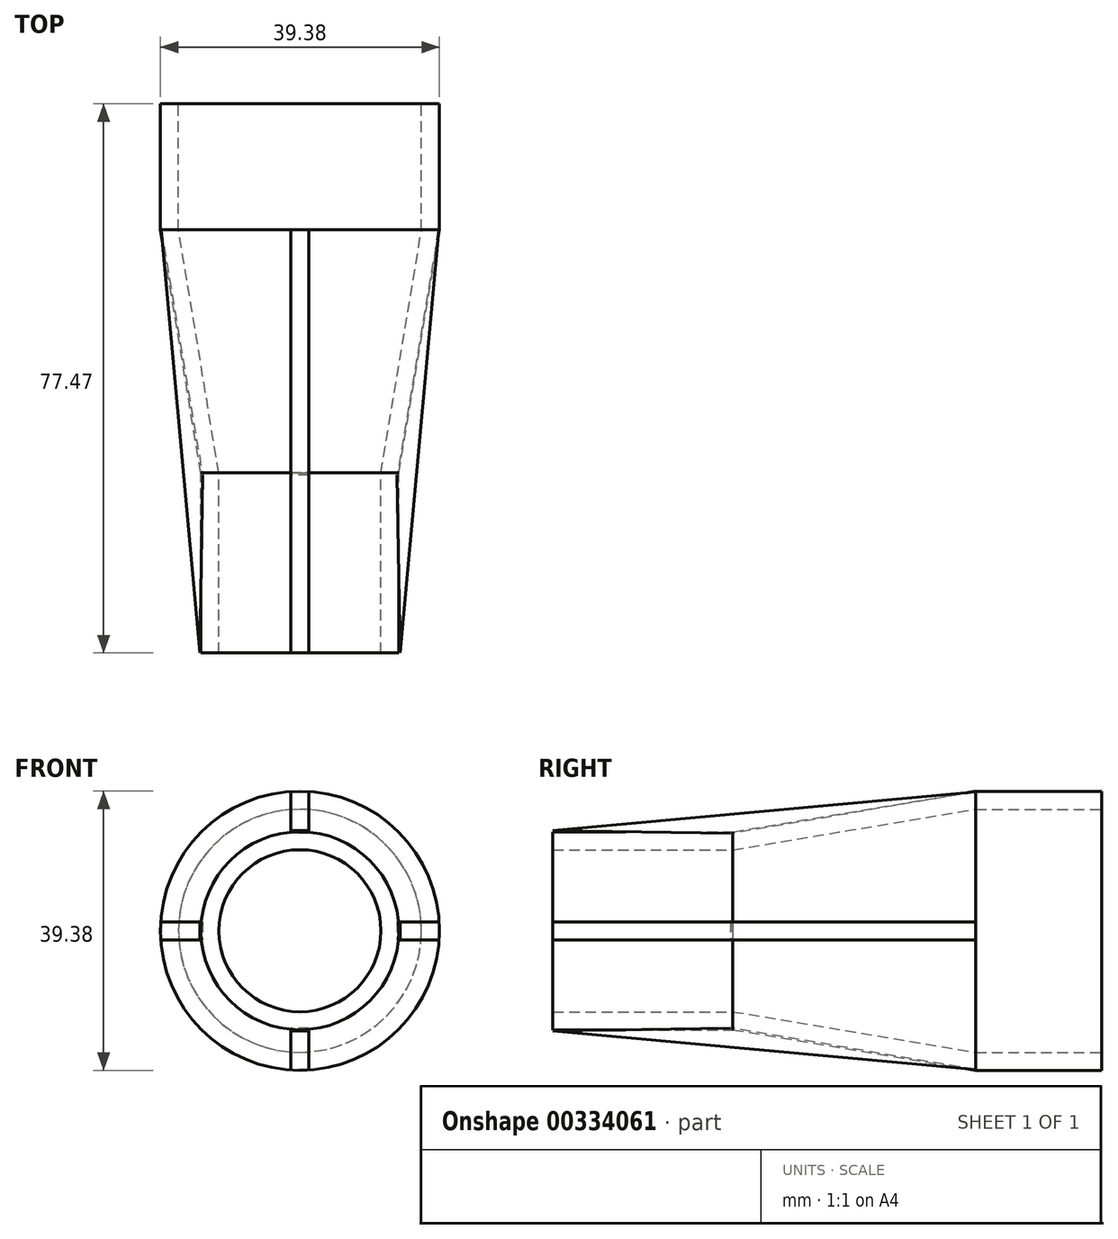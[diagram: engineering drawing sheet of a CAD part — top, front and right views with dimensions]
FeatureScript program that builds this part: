
annotation { "Feature Type Name" : "Feature", "Feature Type Description" : "" }
export const myFeature = defineFeature(function(context is Context, id is Id, definition is map)
    precondition{}
    {
        {
            var Q0;
            Q0=qCreatedBy(makeId("Front.planeOp"),FACE);
            var sketch = newSketch(context, id + "F0", { "sketchPlane" : qUnion([Q0])});
            skCircle(sketch, "E0", {"center": v(0, 0) * mm, "radius": 19.69 * mm});
            skCircle(sketch, "E1", {"center": v(0, 0) * mm, "radius": 17.15 * mm});
            skSolve(sketch);
        }
        {
            var Q0;
            Q0=makeQuery(id+"F0.imprint","IMPRINT",FACE,{"disambiguationData":[TD([[makeQuery(id+"F0.imprint","IMPRINT",EDGE,{"derivedFrom":sQuery(id+"F0.wireOp",EDGE,"E0")}),1.0]])]});
            extrude(context, id + "F1", {"entities" : qUnion([Q0]), "depth" : 17.78 * mm});
        }
        {
            var Q0;
            Q0=qCreatedBy(makeId("Top.planeOp"),FACE);
            var sketch = newSketch(context, id + "F2", { "sketchPlane" : qUnion([Q0])});
            skLineSegment(sketch, "E2", {"start": v(17.15, -17.78) * mm, "end": v(19.69, -17.78) * mm});
            skLineSegment(sketch, "E3.0", {"start": v(11.43, -52.07) * mm, "end": v(13.97, -52.07) * mm});
            skLineSegment(sketch, "E4", {"start": v(11.43, -52.07) * mm, "end": v(11.43, -77.47) * mm});
            skLineSegment(sketch, "E5.0", {"start": v(13.97, -52.07) * mm, "end": v(13.97, -77.47) * mm});
            skLineSegment(sketch, "E6", {"start": v(17.15, -17.78) * mm, "end": v(11.43, -52.07) * mm});
            skLineSegment(sketch, "E7", {"start": v(19.69, -17.78) * mm, "end": v(13.97, -52.07) * mm});
            skLineSegment(sketch, "E8.0", {"start": v(11.43, -77.47) * mm, "end": v(13.97, -77.47) * mm});
            skSolve(sketch);
        }
        {
            var Q0;
            Q0=makeQuery(id+"F2.imprint","IMPRINT",FACE,{"disambiguationData":[TD([[makeQuery(id+"F2.imprint","IMPRINT",EDGE,{"derivedFrom":sQuery(id+"F2.wireOp",EDGE,"E2")}),-1.0]])]});
            var Q1;
            Q1=makeQuery(id+"F2.imprint","IMPRINT",FACE,{"disambiguationData":[TD([[makeQuery(id+"F2.imprint","IMPRINT",EDGE,{"derivedFrom":sQuery(id+"F2.wireOp",EDGE,"E3.0")}),-1.0]])]});
            var Q2;
            Q2=makeQuery(id+"F1.opExtrude","SWEPT_FACE",FACE,{"disambiguationData":[OSD([sQuery(id+"F0.wireOp",EDGE,"E1")])]});
            revolve(context, id + "F3", {"operationType" : NewBodyOperationType.ADD, "entities" : qUnion([Q0, Q1]), "axis" : qUnion([Q2]), "revolveType" : RevolveType.FULL});
        }
        {
            var Q0;
            Q0=qCreatedBy(makeId("Right.planeOp"),FACE);
            var sketch = newSketch(context, id + "F4", { "sketchPlane" : qUnion([Q0])});
            skLineSegment(sketch, "E9", {"start": v(-77.47, 14.14) * mm, "end": v(-17.78, 19.58) * mm});
            skLineSegment(sketch, "E10", {"start": v(-17.78, 19.58) * mm, "end": v(-52.39, 13.72) * mm});
            skLineSegment(sketch, "E11", {"start": v(-52.39, 13.72) * mm, "end": v(-77.47, 14.14) * mm});
            skLineSegment(sketch, "E12.MirrorCS", {"start": v(-77.47, -14.14) * mm, "end": v(-17.78, -19.58) * mm});
            skLineSegment(sketch, "E13.MirrorCS", {"start": v(-52.39, -13.72) * mm, "end": v(-77.47, -14.14) * mm});
            skLineSegment(sketch, "E14.MirrorCS", {"start": v(-17.78, -19.58) * mm, "end": v(-52.39, -13.72) * mm});
            skSolve(sketch);
        }
        {
            var Q0;
            Q0=makeQuery(id+"F4.imprint","IMPRINT",FACE,{"disambiguationData":[TD([[makeQuery(id+"F4.imprint","IMPRINT",EDGE,{"derivedFrom":sQuery(id+"F4.wireOp",EDGE,"E9")}),-1.0]])]});
            var Q1;
            Q1=makeQuery(id+"F4.imprint","IMPRINT",FACE,{"disambiguationData":[TD([[makeQuery(id+"F4.imprint","IMPRINT",EDGE,{"derivedFrom":sQuery(id+"F4.wireOp",EDGE,"E12.MirrorCS")}),1.0]])]});
            extrude(context, id + "F5", {"entities" : qUnion([Q0, Q1]), "endBound" : BoundingType.SYMMETRIC, "depth" : 2.54 * mm});
        }
        {
            var Q0;
            Q0=qCreatedBy(makeId("Right.planeOp"),FACE);
            var sketch = newSketch(context, id + "F6", { "sketchPlane" : qUnion([Q0])});
            skLineSegment(sketch, "E15", {"start": v(0, 0) * mm, "end": v(-87.47, 0) * mm, "construction": true});
            skSolve(sketch);
        }
        {
            var Q0;
            Q0=makeQuery(id+"F5.opExtrude","SWEPT_BODY",BODY,{"disambiguationData":[OSD([sQuery(id+"F4.wireOp",EDGE,"E9"),sQuery(id+"F4.wireOp",EDGE,"E10"),sQuery(id+"F4.wireOp",EDGE,"E11")])]});
            var Q1;
            Q1=makeQuery(id+"F5.opExtrude","SWEPT_BODY",BODY,{"disambiguationData":[OSD([sQuery(id+"F4.wireOp",EDGE,"E12.MirrorCS"),sQuery(id+"F4.wireOp",EDGE,"E13.MirrorCS"),sQuery(id+"F4.wireOp",EDGE,"E14.MirrorCS")])]});
            var Q2;
            Q2=sQuery(id+"F6.wireOp",EDGE,"E15");
            circularPattern(context, id + "F7", {"entities" : qUnion([Q0, Q1]), "axis" : qUnion([Q2]), "angle" : 90 * degree, "instanceCount" : 2, "equalSpace" : true});
        }
    });
